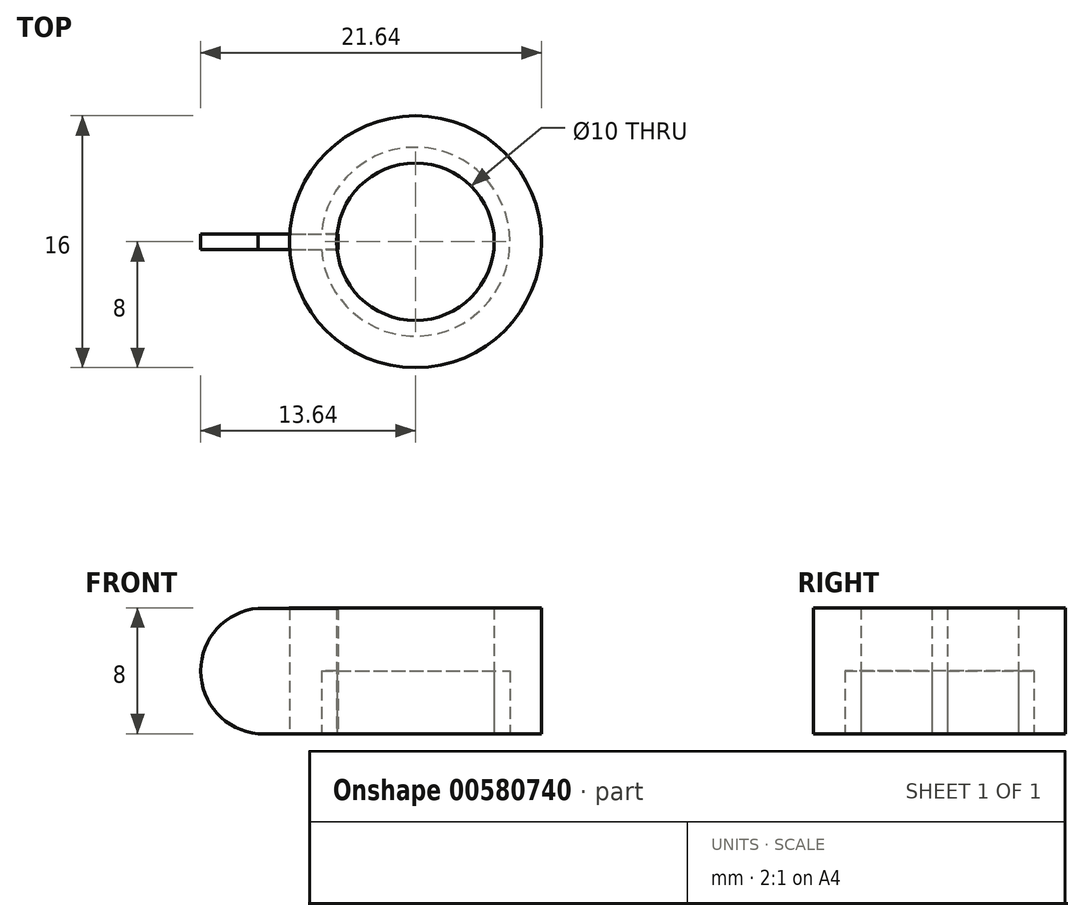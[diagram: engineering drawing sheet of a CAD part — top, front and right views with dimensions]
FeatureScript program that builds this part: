
annotation { "Feature Type Name" : "Feature", "Feature Type Description" : "" }
export const myFeature = defineFeature(function(context is Context, id is Id, definition is map)
    precondition{}
    {
        {
            var Q0;
            Q0=qCreatedBy(makeId("Front.planeOp"),FACE);
            var sketch = newSketch(context, id + "F0", { "sketchPlane" : qUnion([Q0])});
            skLineSegment(sketch, "E0.bottom", {"start": v(-5, 0) * mm, "end": v(-6, 0) * mm});
            skLineSegment(sketch, "E0.top", {"start": v(-5, 4) * mm, "end": v(-6, 4) * mm});
            skLineSegment(sketch, "E0.left", {"start": v(-5, 0) * mm, "end": v(-5, 4) * mm});
            skLineSegment(sketch, "E0.right", {"start": v(-6, 0) * mm, "end": v(-6, 4) * mm});
            skLineSegment(sketch, "E1", {"start": v(0, 0) * mm, "end": v(0, 38.6) * mm});
            skSolve(sketch);
        }
        {
            var Q0;
            Q0=makeQuery(id+"F0.imprint","IMPRINT",FACE,{"disambiguationData":[TD([[makeQuery(id+"F0.imprint","IMPRINT",EDGE,{"derivedFrom":sQuery(id+"F0.wireOp",EDGE,"E0.bottom")}),-1.0]])]});
            var Q1;
            Q1=sQuery(id+"F0.wireOp",EDGE,"E1");
            revolve(context, id + "F1", {"entities" : qUnion([Q0]), "axis" : qUnion([Q1]), "revolveType" : RevolveType.FULL});
        }
        {
            var Q0;
            Q0=qCreatedBy(makeId("Front.planeOp"),FACE);
            var sketch = newSketch(context, id + "F2", { "sketchPlane" : qUnion([Q0])});
            skArc(sketch, "E2", {"start": v(-10, 7.97) * mm, "mid": v(-13.64, 3.98) * mm, "end": v(-10, 0) * mm});
            skLineSegment(sketch, "E3", {"start": v(-10, 7.97) * mm, "end": v(-10, 0) * mm});
            skLineSegment(sketch, "E4.bottom", {"start": v(-10, 7.97) * mm, "end": v(-4.92, 7.97) * mm});
            skLineSegment(sketch, "E4.top", {"start": v(-10, 0) * mm, "end": v(-4.92, 0) * mm});
            skLineSegment(sketch, "E4.right", {"start": v(-4.92, 7.97) * mm, "end": v(-4.92, 0) * mm});
            skPoint(sketch, "E5", {"position": v(-10, 3.98) * mm});
            skSolve(sketch);
        }
        {
            var Q0;
            Q0=qSketchRegion(id+"F2",true);
            extrude(context, id + "F3", {"entities" : qUnion([Q0]), "operationType" : NewBodyOperationType.ADD, "endBound" : BoundingType.SYMMETRIC, "depth" : 1 * mm, "offsetDistance" : 25.4 * mm});
        }
        {
            var Q0;
            Q0=qCreatedBy(makeId("Front.planeOp"),FACE);
            var sketch = newSketch(context, id + "F4", { "sketchPlane" : qUnion([Q0])});
            skLineSegment(sketch, "E6", {"start": v(0, 0) * mm, "end": v(0, 69.09) * mm});
            skSolve(sketch);
        }
        {
            var Q0;
            Q0=qCreatedBy(makeId("Front.planeOp"),FACE);
            var sketch = newSketch(context, id + "F5", { "sketchPlane" : qUnion([Q0])});
            skLineSegment(sketch, "E7.bottom", {"start": v(-5, 8) * mm, "end": v(-8, 8) * mm});
            skLineSegment(sketch, "E7.top", {"start": v(-5, 0) * mm, "end": v(-8, 0) * mm});
            skLineSegment(sketch, "E7.left", {"start": v(-5, 8) * mm, "end": v(-5, 0) * mm});
            skLineSegment(sketch, "E7.right", {"start": v(-8, 8) * mm, "end": v(-8, 0) * mm});
            skLineSegment(sketch, "E8", {"start": v(0, 0) * mm, "end": v(0, 147.64) * mm});
            skSolve(sketch);
        }
        {
            var Q0;
            Q0=makeQuery(id+"F5.imprint","IMPRINT",FACE,{"disambiguationData":[TD([[makeQuery(id+"F5.imprint","IMPRINT",EDGE,{"derivedFrom":sQuery(id+"F5.wireOp",EDGE,"E7.bottom")}),1.0]])]});
            var Q1;
            Q1=sQuery(id+"F5.wireOp",EDGE,"E8");
            revolve(context, id + "F6", {"entities" : qUnion([Q0]), "axis" : qUnion([Q1]), "revolveType" : RevolveType.FULL});
        }
    });
